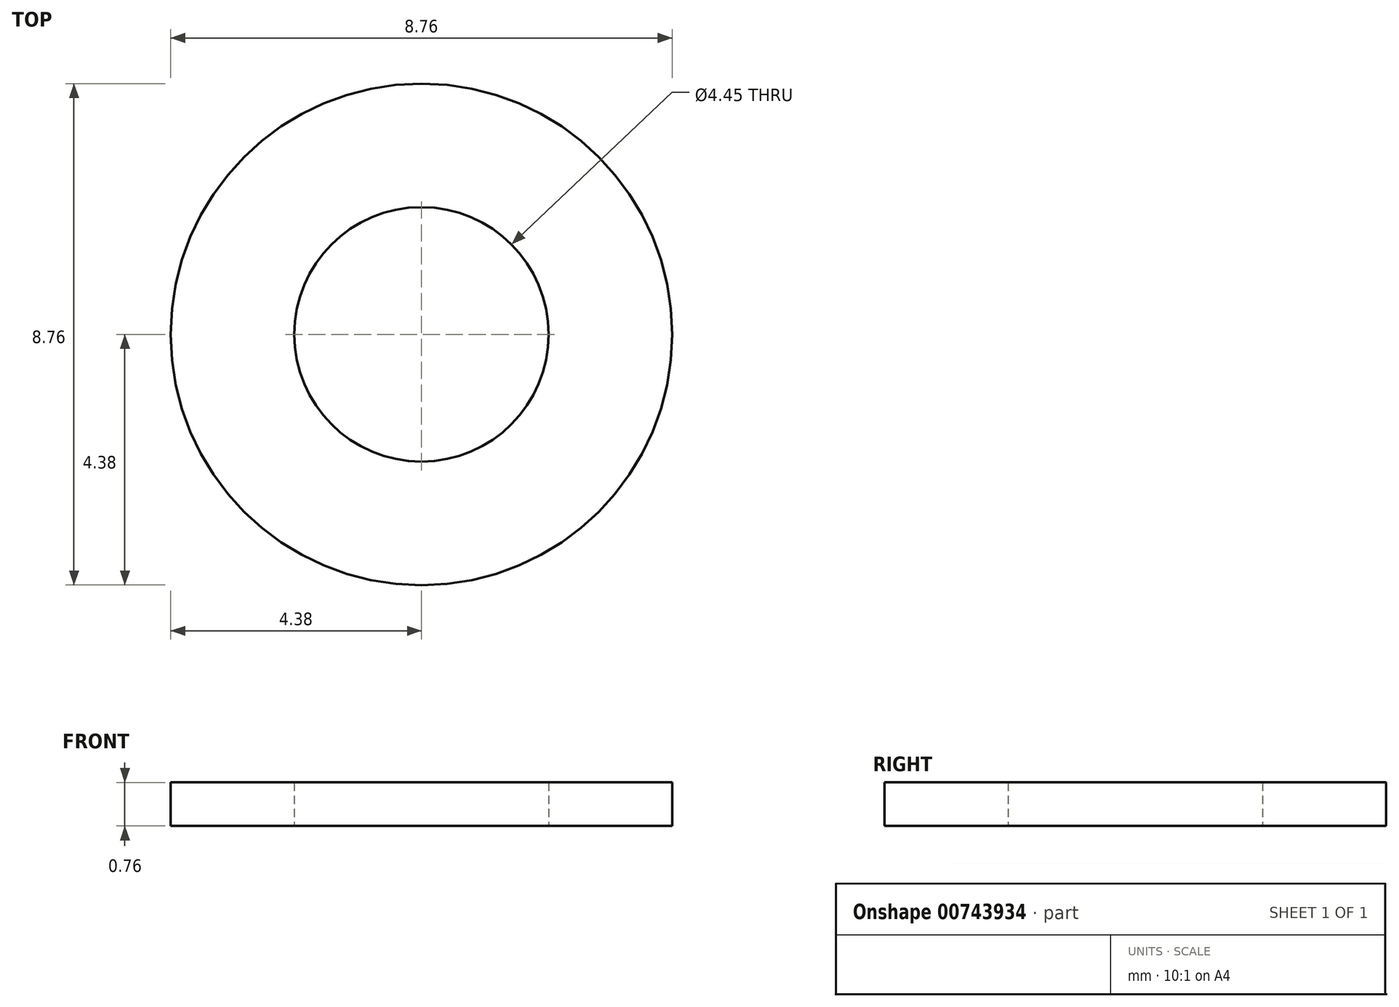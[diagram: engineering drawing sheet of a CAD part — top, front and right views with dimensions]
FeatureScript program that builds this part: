
annotation { "Feature Type Name" : "Feature", "Feature Type Description" : "" }
export const myFeature = defineFeature(function(context is Context, id is Id, definition is map)
    precondition{}
    {
        {
            var Q0;
            Q0=qCreatedBy(makeId("Top.planeOp"),FACE);
            var sketch = newSketch(context, id + "F0", { "sketchPlane" : qUnion([Q0])});
            skCircle(sketch, "E0", {"center": v(0, 0) * mm, "radius": 4.38 * mm});
            skCircle(sketch, "E1", {"center": v(0, 0) * mm, "radius": 2.22 * mm});
            skSolve(sketch);
        }
        {
            var Q0;
            Q0 = qSketchRegion(id + "F0", true);
            extrude(context, id + "F1", {"entities" : qUnion([Q0]), "depth" : 0.76 * mm, "offsetDistance" : 25.4 * mm});
        }
    });
